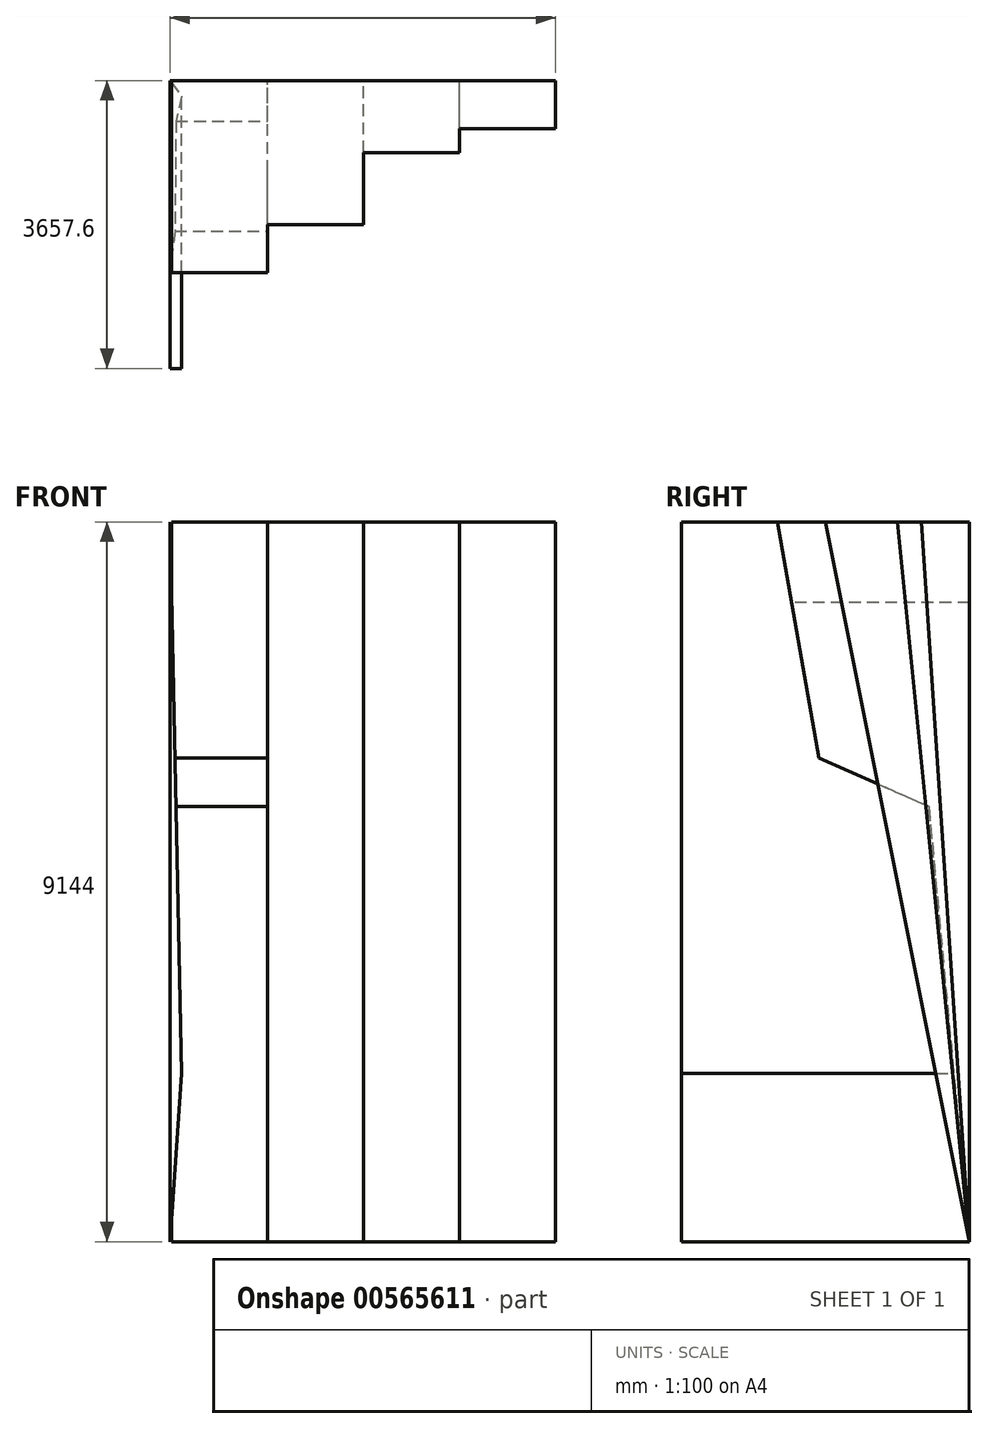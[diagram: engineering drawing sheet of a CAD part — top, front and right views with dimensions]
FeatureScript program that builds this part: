
annotation { "Feature Type Name" : "Feature", "Feature Type Description" : "" }
export const myFeature = defineFeature(function(context is Context, id is Id, definition is map)
    precondition{}
    {
        {
            var Q0;
            Q0=qCreatedBy(makeId("Right.planeOp"),FACE);
            var sketch = newSketch(context, id + "F0", { "sketchPlane" : qUnion([Q0])});
            skLineSegment(sketch, "E0", {"start": v(0, 0) * mm, "end": v(0, 9144) * mm});
            skLineSegment(sketch, "E1", {"start": v(0, 9144) * mm, "end": v(-609.6, 9144) * mm});
            skLineSegment(sketch, "E2", {"start": v(-609.6, 9144) * mm, "end": v(0, 0) * mm});
            skSolve(sketch);
        }
        {
            var Q0;
            Q0=makeQuery(id+"F0.imprint","IMPRINT",FACE,{"disambiguationData":[TD([[makeQuery(id+"F0.imprint","IMPRINT",EDGE,{"derivedFrom":sQuery(id+"F0.wireOp",EDGE,"E0")}),1.0]])]});
            extrude(context, id + "F1", {"entities" : qUnion([Q0]), "depth" : 1219.2 * mm, "offsetDistance" : 25.4 * mm});
        }
        {
            var Q0;
            Q0=qCreatedBy(makeId("Right.planeOp"),FACE);
            var sketch = newSketch(context, id + "F2", { "sketchPlane" : qUnion([Q0])});
            skLineSegment(sketch, "E3", {"start": v(0, 0) * mm, "end": v(0, 9144) * mm});
            skLineSegment(sketch, "E4", {"start": v(0, 9144) * mm, "end": v(-914.4, 9144) * mm});
            skLineSegment(sketch, "E5", {"start": v(-914.4, 9144) * mm, "end": v(0, 0) * mm});
            skSolve(sketch);
        }
        {
            var Q0;
            Q0 = qSketchRegion(id + "F2", true);
            extrude(context, id + "F3", {"entities" : qUnion([Q0]), "operationType" : NewBodyOperationType.ADD, "oppositeDirection" : true, "depth" : 1219.2 * mm, "offsetDistance" : 25.4 * mm, "hasSecondDirection" : true, "secondDirectionOppositeDirection" : false, "secondDirectionDepth" : 0 * mm});
        }
        {
            var Q0;
            Q0=qCreatedBy(makeId("Right.planeOp"),FACE);
            var sketch = newSketch(context, id + "F4", { "sketchPlane" : qUnion([Q0])});
            skLineSegment(sketch, "E6", {"start": v(0, 0) * mm, "end": v(0, 9144) * mm});
            skLineSegment(sketch, "E7", {"start": v(0, 9144) * mm, "end": v(-1828.8, 9144) * mm});
            skLineSegment(sketch, "E8", {"start": v(-1828.8, 9144) * mm, "end": v(0, 0) * mm});
            skSolve(sketch);
        }
        {
            var Q0;
            Q0 = qSketchRegion(id + "F4", true);
            extrude(context, id + "F5", {"entities" : qUnion([Q0]), "operationType" : NewBodyOperationType.ADD, "oppositeDirection" : true, "depth" : 2438.4 * mm, "offsetDistance" : 25.4 * mm, "hasSecondDirection" : true, "secondDirectionOppositeDirection" : true, "secondDirectionDepth" : 1219.2 * mm});
        }
        {
            var Q0;
            Q0=qCreatedBy(makeId("Right.planeOp"),FACE);
            var sketch = newSketch(context, id + "F6", { "sketchPlane" : qUnion([Q0])});
            skLineSegment(sketch, "E9", {"start": v(0, 0) * mm, "end": v(0, 9144) * mm});
            skLineSegment(sketch, "E10", {"start": v(0, 9144) * mm, "end": v(-2438.4, 9144) * mm});
            skLineSegment(sketch, "E11", {"start": v(-2438.4, 9144) * mm, "end": v(-1911.29, 6141.92) * mm});
            skLineSegment(sketch, "E12", {"start": v(-1911.29, 6141.92) * mm, "end": v(-516.6, 5527.6) * mm});
            skLineSegment(sketch, "E13", {"start": v(-516.6, 5527.6) * mm, "end": v(0, 0) * mm});
            skSolve(sketch);
        }
        {
            var Q0;
            Q0 = qSketchRegion(id + "F6", true);
            extrude(context, id + "F7", {"entities" : qUnion([Q0]), "operationType" : NewBodyOperationType.ADD, "oppositeDirection" : true, "depth" : 3657.6 * mm, "offsetDistance" : 25.4 * mm, "hasSecondDirection" : true, "secondDirectionOppositeDirection" : true, "secondDirectionDepth" : 2438.4 * mm});
        }
        {
            var Q0;
            Q0=qCreatedBy(makeId("Front.planeOp"),FACE);
            var sketch = newSketch(context, id + "F8", { "sketchPlane" : qUnion([Q0])});
            skLineSegment(sketch, "E14", {"start": v(-3679.18, 0) * mm, "end": v(-3679.18, 9144) * mm});
            skLineSegment(sketch, "E15", {"start": v(-3679.18, 9144) * mm, "end": v(-3531.74, 2135.15) * mm});
            skLineSegment(sketch, "E16", {"start": v(-3531.74, 2135.15) * mm, "end": v(-3679.18, 0) * mm});
            skSolve(sketch);
        }
        {
            var Q0;
            Q0 = qSketchRegion(id + "F8", true);
            extrude(context, id + "F9", {"entities" : qUnion([Q0]), "operationType" : NewBodyOperationType.ADD, "depth" : 3657.6 * mm, "offsetDistance" : 25.4 * mm, "hasSecondDirection" : true, "secondDirectionOppositeDirection" : true, "secondDirectionDepth" : 0 * mm});
        }
    });
